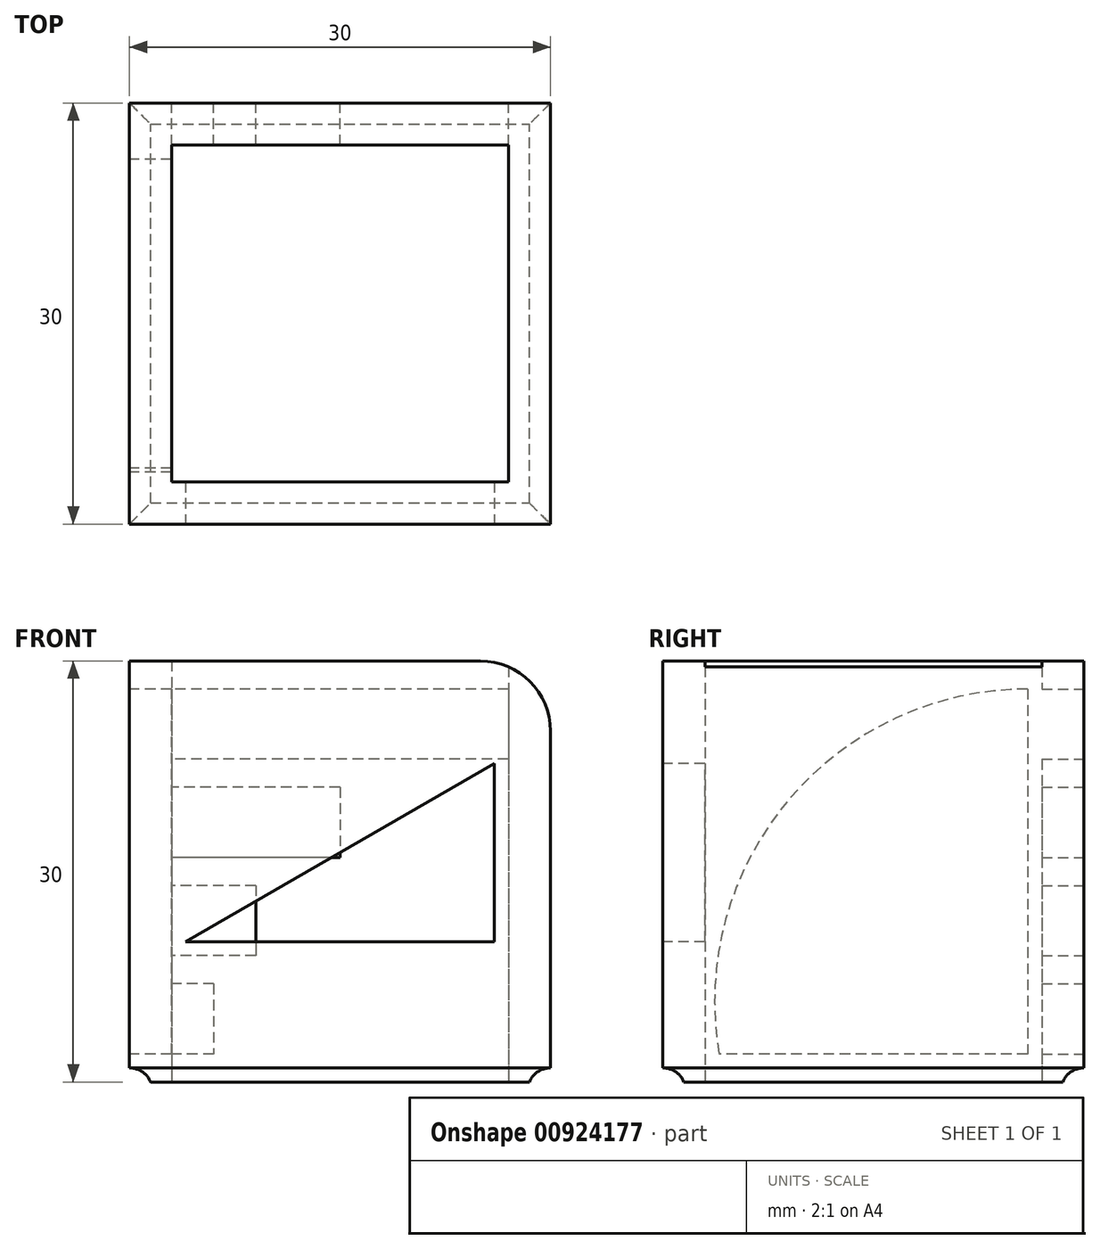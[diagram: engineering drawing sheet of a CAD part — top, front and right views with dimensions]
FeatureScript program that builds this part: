
annotation { "Feature Type Name" : "Feature", "Feature Type Description" : "" }
export const myFeature = defineFeature(function(context is Context, id is Id, definition is map)
    precondition{}
    {
        {
            var Q0;
            Q0=qCreatedBy(makeId("Top.planeOp"),FACE);
            var sketch = newSketch(context, id + "F0", { "sketchPlane" : qUnion([Q0])});
            skLineSegment(sketch, "E0.bottom", {"start": v(-15, 15) * mm, "end": v(15, 15) * mm});
            skLineSegment(sketch, "E0.top", {"start": v(-15, -15) * mm, "end": v(15, -15) * mm});
            skLineSegment(sketch, "E0.left", {"start": v(-15, 15) * mm, "end": v(-15, -15) * mm});
            skLineSegment(sketch, "E0.right", {"start": v(15, 15) * mm, "end": v(15, -15) * mm});
            skLineSegment(sketch, "E1.bottom", {"start": v(-12, 12) * mm, "end": v(12, 12) * mm});
            skLineSegment(sketch, "E1.top", {"start": v(-12, -12) * mm, "end": v(12, -12) * mm});
            skLineSegment(sketch, "E1.left", {"start": v(-12, 12) * mm, "end": v(-12, -12) * mm});
            skLineSegment(sketch, "E1.right", {"start": v(12, 12) * mm, "end": v(12, -12) * mm});
            skSolve(sketch);
        }
        {
            var Q0;
            Q0=qSketchRegion(id+"F0",true);
            extrude(context, id + "F1", {"entities" : qUnion([Q0]), "depth" : 30 * mm, "offsetDistance" : 25 * mm});
        }
        {
            var Q0;
            Q0=makeQuery(id+"F1.opExtrude","SWEPT_FACE",FACE,{"disambiguationData":[OSD([sQuery(id+"F0.wireOp",EDGE,"E0.top")])]});
            var sketch = newSketch(context, id + "F2", { "sketchPlane" : qUnion([Q0])});
            skLineSegment(sketch, "E2", {"start": v(-11, 10) * mm, "end": v(11, 10) * mm});
            skLineSegment(sketch, "E3", {"start": v(11, 10) * mm, "end": v(11, 22.7) * mm});
            skLineSegment(sketch, "E4", {"start": v(11, 22.7) * mm, "end": v(-11, 10) * mm});
            skSolve(sketch);
        }
        {
            var Q0;
            Q0=qSketchRegion(id+"F2",true);
            extrude(context, id + "F3", {"entities" : qUnion([Q0]), "operationType" : NewBodyOperationType.REMOVE, "oppositeDirection" : true, "depth" : 5 * mm, "offsetDistance" : 25 * mm});
        }
        {
            var Q0;
            Q0=makeQuery(id+"F1.opExtrude","SWEPT_FACE",FACE,{"disambiguationData":[OSD([sQuery(id+"F0.wireOp",EDGE,"E0.left")])]});
            var sketch = newSketch(context, id + "F4", { "sketchPlane" : qUnion([Q0])});
            skLineSegment(sketch, "E5", {"start": v(-11, 28) * mm, "end": v(-11, 2) * mm});
            skLineSegment(sketch, "E6", {"start": v(-11, 2) * mm, "end": v(11, 2) * mm});
            skArc(sketch, "E7", {"start": v(11, 2) * mm, "mid": v(6.03, 20.1) * mm, "end": v(-11, 28) * mm});
            skLineSegment(sketch, "E8", {"start": v(-11, 28) * mm, "end": v(1.96, 28) * mm, "construction": true});
            skSolve(sketch);
        }
        {
            var Q0;
            Q0=qSketchRegion(id+"F4",true);
            extrude(context, id + "F5", {"entities" : qUnion([Q0]), "operationType" : NewBodyOperationType.REMOVE, "oppositeDirection" : true, "depth" : 4 * mm, "offsetDistance" : 25 * mm});
        }
        {
            var Q0;
            Q0=makeQuery(id+"F1.opExtrude","SWEPT_FACE",FACE,{"disambiguationData":[OSD([sQuery(id+"F0.wireOp",EDGE,"E0.bottom")])]});
            var sketch = newSketch(context, id + "F6", { "sketchPlane" : qUnion([Q0])});
            skLineSegment(sketch, "E9.bottom", {"start": v(0, 16) * mm, "end": v(12, 16) * mm});
            skLineSegment(sketch, "E9.top", {"start": v(0, 21) * mm, "end": v(12, 21) * mm});
            skLineSegment(sketch, "E9.left", {"start": v(0, 21) * mm, "end": v(0, 16) * mm});
            skLineSegment(sketch, "E9.right", {"start": v(12, 21) * mm, "end": v(12, 16) * mm});
            skLineSegment(sketch, "E10.bottom", {"start": v(6, 14) * mm, "end": v(12, 14) * mm});
            skLineSegment(sketch, "E10.top", {"start": v(6, 9) * mm, "end": v(12, 9) * mm});
            skLineSegment(sketch, "E10.left", {"start": v(6, 14) * mm, "end": v(6, 9) * mm});
            skLineSegment(sketch, "E10.right", {"start": v(12, 14) * mm, "end": v(12, 9) * mm});
            skLineSegment(sketch, "E11.bottom", {"start": v(9, 7) * mm, "end": v(12, 7) * mm});
            skLineSegment(sketch, "E11.top", {"start": v(9, 2) * mm, "end": v(12, 2) * mm});
            skLineSegment(sketch, "E11.left", {"start": v(9, 7) * mm, "end": v(9, 2) * mm});
            skLineSegment(sketch, "E11.right", {"start": v(12, 7) * mm, "end": v(12, 2) * mm});
            skLineSegment(sketch, "E12", {"start": v(9, 9) * mm, "end": v(9, 7) * mm, "construction": true});
            skLineSegment(sketch, "E13", {"start": v(6, 16) * mm, "end": v(6, 14) * mm, "construction": true});
            skLineSegment(sketch, "E14.bottom", {"start": v(-12, 28) * mm, "end": v(12, 28) * mm});
            skLineSegment(sketch, "E14.top", {"start": v(-12, 23) * mm, "end": v(12, 23) * mm});
            skLineSegment(sketch, "E14.left", {"start": v(-12, 28) * mm, "end": v(-12, 23) * mm});
            skLineSegment(sketch, "E14.right", {"start": v(12, 28) * mm, "end": v(12, 23) * mm});
            skLineSegment(sketch, "E15", {"start": v(0, 21) * mm, "end": v(0, 23) * mm, "construction": true});
            skSolve(sketch);
        }
        {
            var Q0;
            Q0=qSketchRegion(id+"F6",true);
            extrude(context, id + "F7", {"entities" : qUnion([Q0]), "operationType" : NewBodyOperationType.REMOVE, "oppositeDirection" : true, "depth" : 3 * mm, "offsetDistance" : 25 * mm});
        }
        {
            var Q0;
            Q0=makeQuery(id+"F1.opExtrude","CAP_FACE",FACE,{"disambiguationData":[OSD([sQuery(id+"F0.wireOp",EDGE,"E0.bottom"),sQuery(id+"F0.wireOp",EDGE,"E0.top"),sQuery(id+"F0.wireOp",EDGE,"E0.left"),sQuery(id+"F0.wireOp",EDGE,"E0.right"),sQuery(id+"F0.wireOp",EDGE,"E1.bottom"),sQuery(id+"F0.wireOp",EDGE,"E1.top"),sQuery(id+"F0.wireOp",EDGE,"E1.left"),sQuery(id+"F0.wireOp",EDGE,"E1.right")])],"isStart":true});
            var sketch = newSketch(context, id + "F8", { "sketchPlane" : qUnion([Q0])});
            skLineSegment(sketch, "E16.bottom", {"start": v(-13.5, 13.5) * mm, "end": v(13.5, 13.5) * mm});
            skLineSegment(sketch, "E16.top", {"start": v(-13.5, -13.5) * mm, "end": v(13.5, -13.5) * mm});
            skLineSegment(sketch, "E16.left", {"start": v(-13.5, 13.5) * mm, "end": v(-13.5, -13.5) * mm});
            skLineSegment(sketch, "E16.right", {"start": v(13.5, 13.5) * mm, "end": v(13.5, -13.5) * mm});
            skLineSegment(sketch, "E17.bottom", {"start": v(-15.4, -15.4) * mm, "end": v(15.4, -15.4) * mm});
            skLineSegment(sketch, "E17.top", {"start": v(-15.4, 15.4) * mm, "end": v(15.4, 15.4) * mm});
            skLineSegment(sketch, "E17.left", {"start": v(-15.4, 15.4) * mm, "end": v(-15.4, -15.4) * mm});
            skLineSegment(sketch, "E17.right", {"start": v(15.4, 15.4) * mm, "end": v(15.4, -15.4) * mm});
            skSolve(sketch);
        }
        {
            var Q0;
            Q0=qSketchRegion(id+"F8",true);
            extrude(context, id + "F9", {"entities" : qUnion([Q0]), "operationType" : NewBodyOperationType.REMOVE, "oppositeDirection" : true, "depth" : 1 * mm, "offsetDistance" : 25 * mm});
        }
        {
            var Q0;
            Q0=makeQuery(id+"F9.boolean.opBoolean","COPY",EDGE,{"derivedFrom":makeQuery(id+"F9.opExtrude","CAP_EDGE",EDGE,{"disambiguationData":[OSD([sQuery(id+"F8.wireOp",EDGE,"E16.left")])],"isStart":false})});
            var Q1;
            Q1=makeQuery(id+"F9.boolean.opBoolean","COPY",EDGE,{"derivedFrom":makeQuery(id+"F9.opExtrude","CAP_EDGE",EDGE,{"disambiguationData":[OSD([sQuery(id+"F8.wireOp",EDGE,"E16.top")])],"isStart":false})});
            var Q2;
            Q2=makeQuery(id+"F9.boolean.opBoolean","COPY",EDGE,{"derivedFrom":makeQuery(id+"F9.opExtrude","CAP_EDGE",EDGE,{"disambiguationData":[OSD([sQuery(id+"F8.wireOp",EDGE,"E16.right")])],"isStart":false})});
            var Q3;
            Q3=makeQuery(id+"F9.boolean.opBoolean","COPY",EDGE,{"derivedFrom":makeQuery(id+"F9.opExtrude","CAP_EDGE",EDGE,{"disambiguationData":[OSD([sQuery(id+"F8.wireOp",EDGE,"E16.bottom")])],"isStart":false})});
            fillet(context, id + "F10", {"entities" : qUnion([Q0, Q1, Q2, Q3]), "radius" : 1.6 * mm, "tangentPropagation" : true, "allowEdgeOverflow" : false});
        }
        {
            var Q0;
            Q0=makeQuery(id+"F1.opExtrude","CAP_EDGE",EDGE,{"disambiguationData":[OSD([sQuery(id+"F0.wireOp",EDGE,"E0.right")])],"isStart":false});
            fillet(context, id + "F11", {"entities" : qUnion([Q0]), "radius" : 5 * mm, "tangentPropagation" : true, "allowEdgeOverflow" : false});
        }
    });
